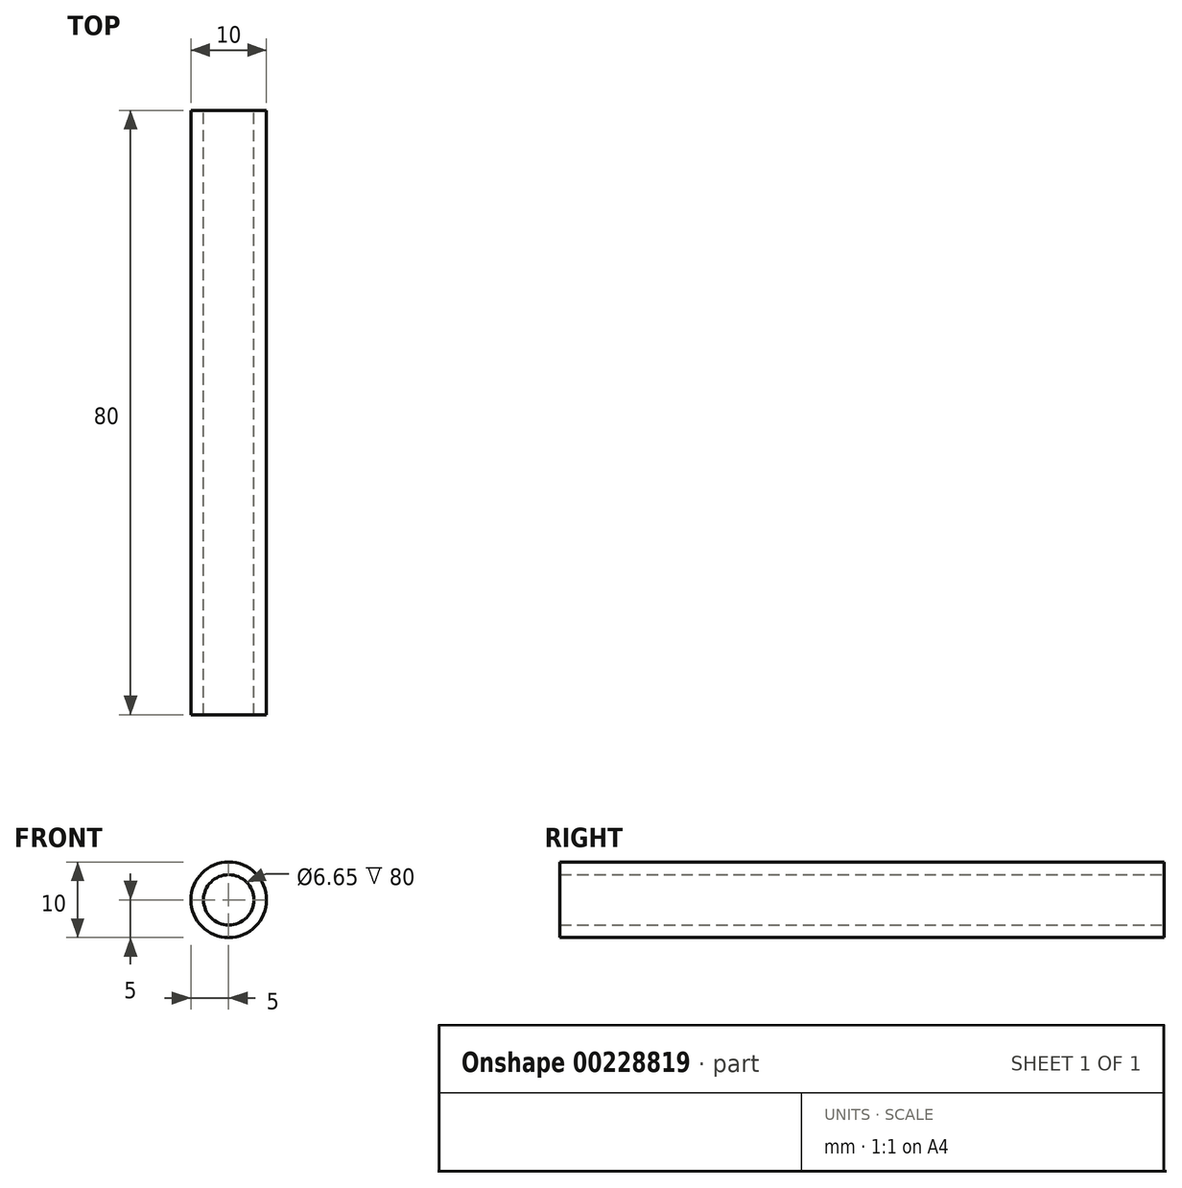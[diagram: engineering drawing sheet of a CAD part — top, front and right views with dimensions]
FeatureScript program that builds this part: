
annotation { "Feature Type Name" : "Feature", "Feature Type Description" : "" }
export const myFeature = defineFeature(function(context is Context, id is Id, definition is map)
    precondition{}
    {
        {
            var Q0;
            Q0=qCreatedBy(makeId("Front.planeOp"),FACE);
            var sketch = newSketch(context, id + "F0", { "sketchPlane" : qUnion([Q0])});
            skCircle(sketch, "E0", {"center": v(0, 0) * mm, "radius": 3.32 * mm});
            skCircle(sketch, "E1", {"center": v(0, 0) * mm, "radius": 5 * mm});
            skSolve(sketch);
        }
        {
            var Q0;
            Q0 = qSketchRegion(id + "F0", true);
            extrude(context, id + "F1", {"entities" : qUnion([Q0]), "depth" : (20 + 20) * mm, "hasSecondDirection" : true, "secondDirectionOppositeDirection" : true, "secondDirectionDepth" : (20 + 20) * mm});
        }
    });
